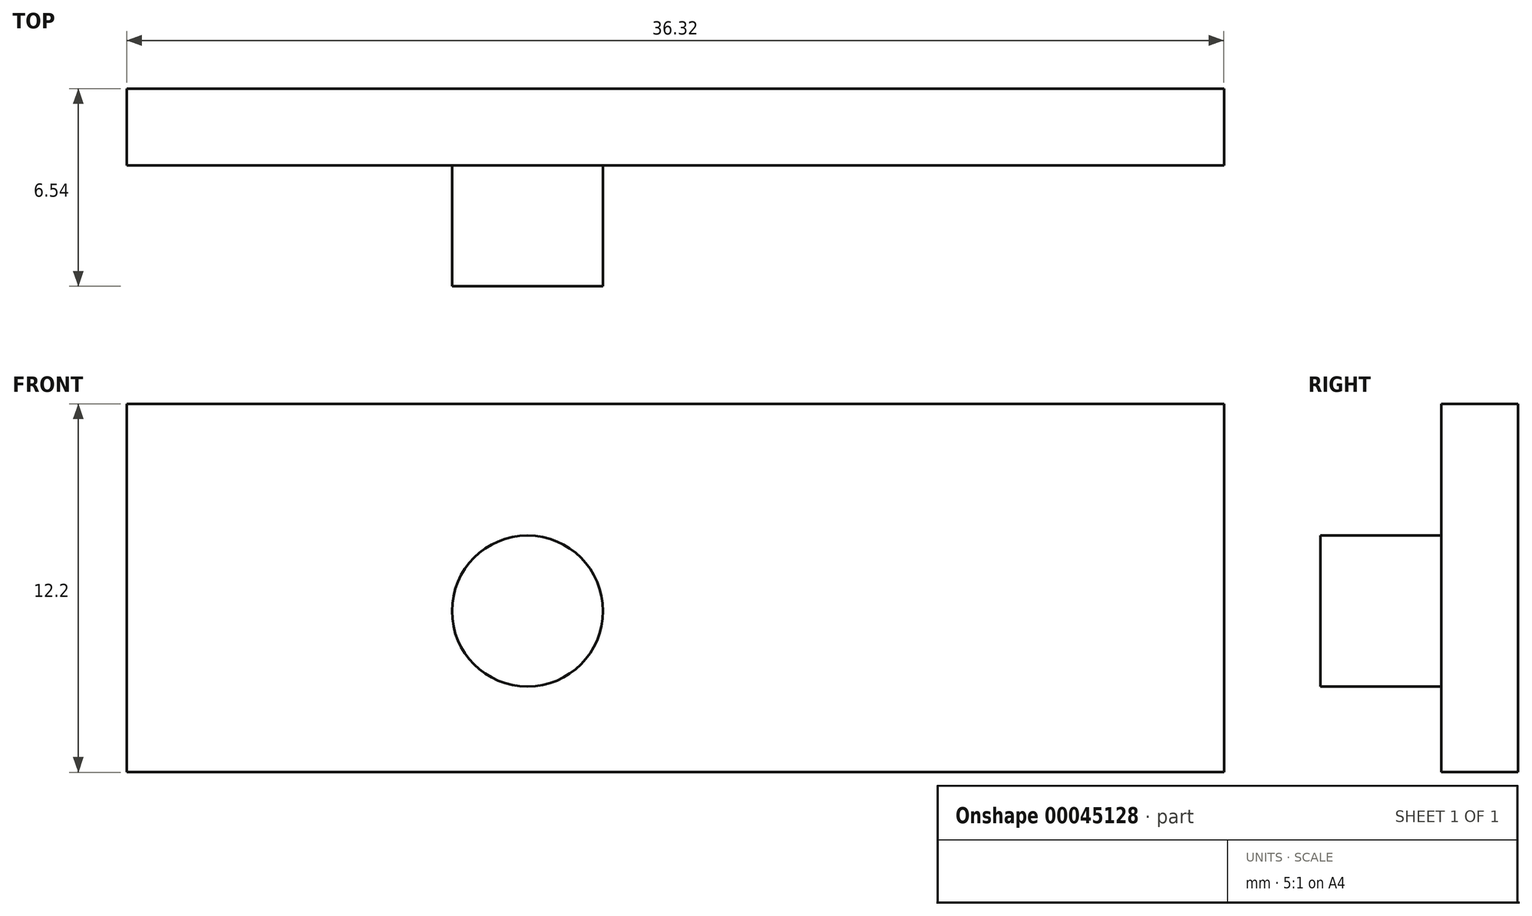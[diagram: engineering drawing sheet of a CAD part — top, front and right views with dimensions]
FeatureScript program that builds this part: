
annotation { "Feature Type Name" : "Feature", "Feature Type Description" : "" }
export const myFeature = defineFeature(function(context is Context, id is Id, definition is map)
    precondition{}
    {
        {
            var Q0;
            Q0=qCreatedBy(makeId("Front.planeOp"),FACE);
            var sketch = newSketch(context, id + "F0", { "sketchPlane" : qUnion([Q0])});
            skLineSegment(sketch, "E0.rect.bottom", {"start": v(-18.16, 6.1) * mm, "end": v(18.16, 6.1) * mm});
            skLineSegment(sketch, "E0.rect.top", {"start": v(-18.16, -6.1) * mm, "end": v(18.16, -6.1) * mm});
            skLineSegment(sketch, "E0.rect.left", {"start": v(-18.16, 6.1) * mm, "end": v(-18.16, -6.1) * mm});
            skLineSegment(sketch, "E0.rect.right", {"start": v(18.16, 6.1) * mm, "end": v(18.16, -6.1) * mm});
            skPoint(sketch, "E0.rect.middle", {"position": v(0, 0) * mm});
            skSolve(sketch);
        }
        {
            var Q0;
            Q0=makeQuery(id+"F0.imprint","IMPRINT",FACE,{"disambiguationData":[TD([[makeQuery(id+"F0.imprint","IMPRINT",EDGE,{"derivedFrom":sQuery(id+"F0.wireOp",EDGE,"E0.rect.bottom")}),-1.0]])]});
            extrude(context, id + "F1", {"entities" : qUnion([Q0]), "depth" : 2.54 * mm});
        }
        {
            var Q0;
            Q0=makeQuery(id+"F1.opExtrude","CAP_FACE",FACE,{"disambiguationData":[OSD([sQuery(id+"F0.wireOp",EDGE,"E0.rect.bottom"),sQuery(id+"F0.wireOp",EDGE,"E0.rect.top"),sQuery(id+"F0.wireOp",EDGE,"E0.rect.left"),sQuery(id+"F0.wireOp",EDGE,"E0.rect.right")])],"isStart":false});
            var sketch = newSketch(context, id + "F2", { "sketchPlane" : qUnion([Q0])});
            skLineSegment(sketch, "E1", {"start": v(-18.16, -0.76) * mm, "end": v(-4.9, -0.76) * mm});
            skLineSegment(sketch, "E2", {"start": v(-4.9, -0.76) * mm, "end": v(-4.9, 6.1) * mm});
            skCircle(sketch, "E3", {"center": v(-4.9, -0.76) * mm, "radius": 2.5 * mm});
            skSolve(sketch);
        }
        {
            var Q0;
            Q0 = qSketchRegion(id + "F2", true);
            extrude(context, id + "F3", {"entities" : qUnion([Q0]), "operationType" : NewBodyOperationType.ADD, "depth" : 4 * mm});
        }
    });
